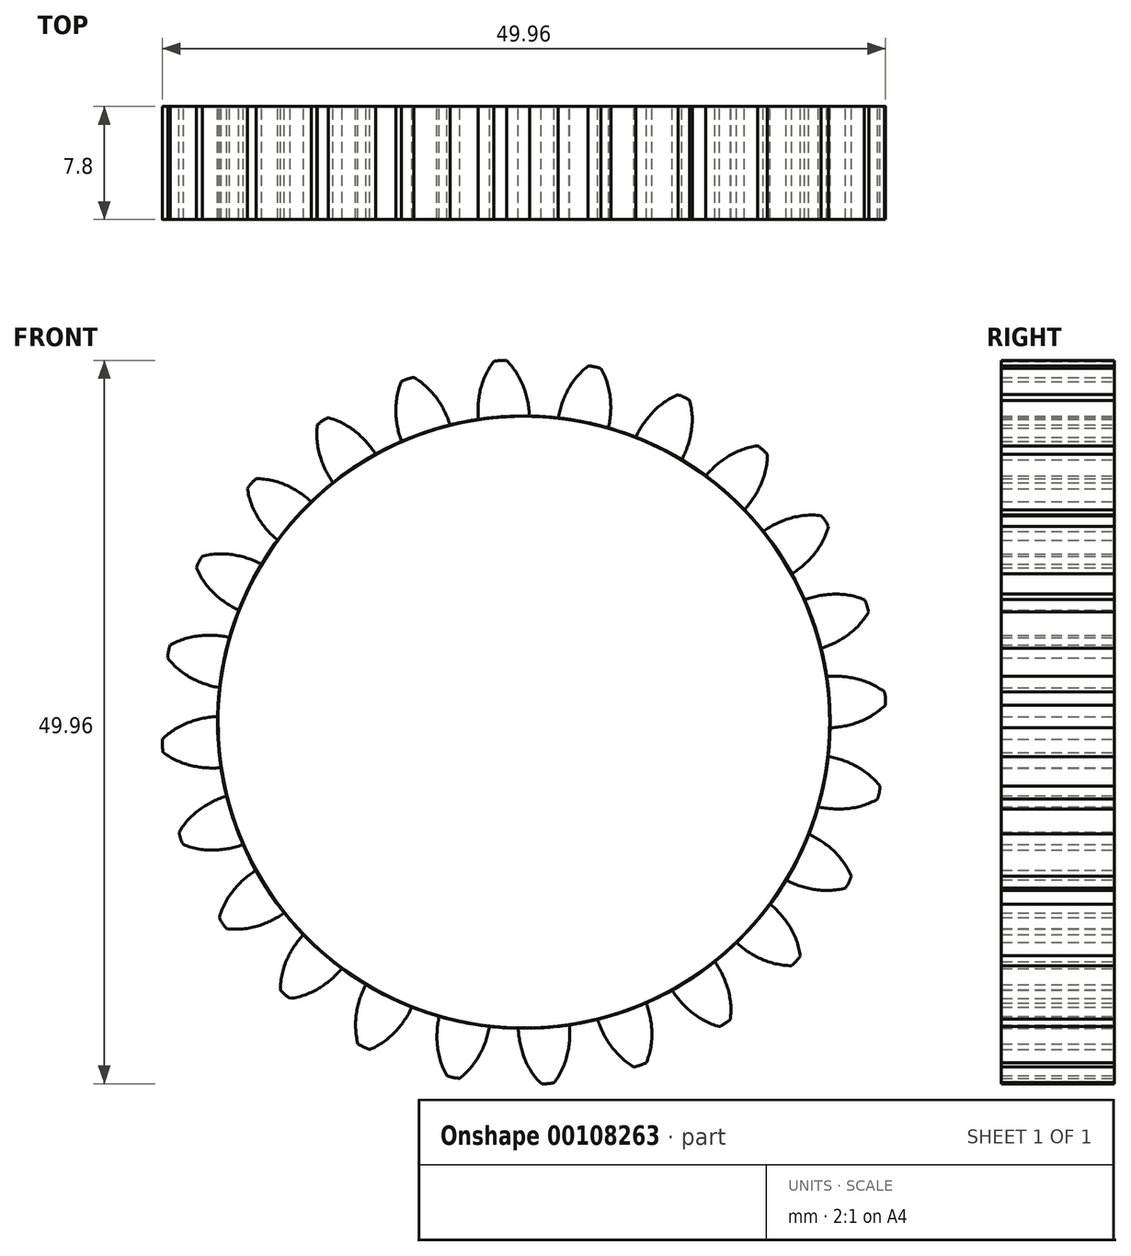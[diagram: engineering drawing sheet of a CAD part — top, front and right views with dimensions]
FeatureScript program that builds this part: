
annotation { "Feature Type Name" : "Feature", "Feature Type Description" : "" }
export const myFeature = defineFeature(function(context is Context, id is Id, definition is map)
    precondition{}
    {
        {
            var Q0;
            Q0=qCreatedBy(makeId("Front.planeOp"),FACE);
            var sketch = newSketch(context, id + "F0", { "sketchPlane" : qUnion([Q0])});
            skCircle(sketch, "E0", {"center": v(0, 0) * mm, "radius": 21.15 * mm});
            skCircle(sketch, "E1", {"center": v(0, 0) * mm, "radius": 23.1 * mm, "construction": true});
            skCircle(sketch, "E2", {"center": v(0, 0) * mm, "radius": 25 * mm, "construction": true});
            skLineSegment(sketch, "E3", {"start": v(0, 0) * mm, "end": v(0, 32.42) * mm, "construction": true});
            skLineSegment(sketch, "E4", {"start": v(0, 0) * mm, "end": v(-2.18, 33.2) * mm, "construction": true});
            skLineSegment(sketch, "E5", {"start": v(0, 23.1) * mm, "end": v(-25.09, 23.1) * mm, "construction": true});
            skLineSegment(sketch, "E6", {"start": v(0, 23.1) * mm, "end": v(-24.37, 14.23) * mm, "construction": true});
            skCircle(sketch, "E7", {"center": v(0, 23.1) * mm, "radius": 5.75 * mm, "construction": true});
            skCircle(sketch, "E8", {"center": v(0, 0) * mm, "radius": 21.7 * mm, "construction": true});
            skCircle(sketch, "E9", {"center": v(-5.36, 21.02) * mm, "radius": 5.75 * mm, "construction": true});
            skArc(sketch, "E10", {"start": v(0, 23.1) * mm, "mid": v(-0.5, 24.1) * mm, "end": v(-1.18, 24.97) * mm});
            skArc(sketch, "E11", {"start": v(0.39, 21.15) * mm, "mid": v(0.27, 22.14) * mm, "end": v(0, 23.1) * mm});
            skArc(sketch, "E12.MirrorCS", {"start": v(-3.02, 22.9) * mm, "mid": v(-2.66, 23.96) * mm, "end": v(-2.09, 24.91) * mm});
            skArc(sketch, "E13.MirrorCS", {"start": v(-3.14, 20.92) * mm, "mid": v(-3.16, 21.91) * mm, "end": v(-3.02, 22.9) * mm});
            skArc(sketch, "E14", {"start": v(-1.18, 24.97) * mm, "mid": v(-1.64, 24.98) * mm, "end": v(-2.09, 24.91) * mm});
            skSolve(sketch);
        }
        {
            var Q0;
            Q0 = qSketchRegion(id + "F0", true);
            extrude(context, id + "F1", {"entities" : qUnion([Q0]), "depth" : 7.8 * mm});
        }
        {
            var Q0;
            Q0=makeQuery(id+"F1.opExtrude","SWEPT_BODY",BODY,{"disambiguationData":[OSD([sQuery(id+"F0.wireOp",EDGE,"E0"),sQuery(id+"F0.wireOp",EDGE,"E10"),sQuery(id+"F0.wireOp",EDGE,"E11"),sQuery(id+"F0.wireOp",EDGE,"E12.MirrorCS"),sQuery(id+"F0.wireOp",EDGE,"E13.MirrorCS"),sQuery(id+"F0.wireOp",EDGE,"E14")])]});
            var Q1;
            Q1=makeQuery(id+"F1.opExtrude","SWEPT_FACE",FACE,{"disambiguationData":[OSD([sQuery(id+"F0.wireOp",EDGE,"E0")])]});
            circularPattern(context, id + "F2", {"entities" : qUnion([Q0]), "axis" : qUnion([Q1]), "angle" : 15 * degree, "instanceCount" : 24});
        }
    });
